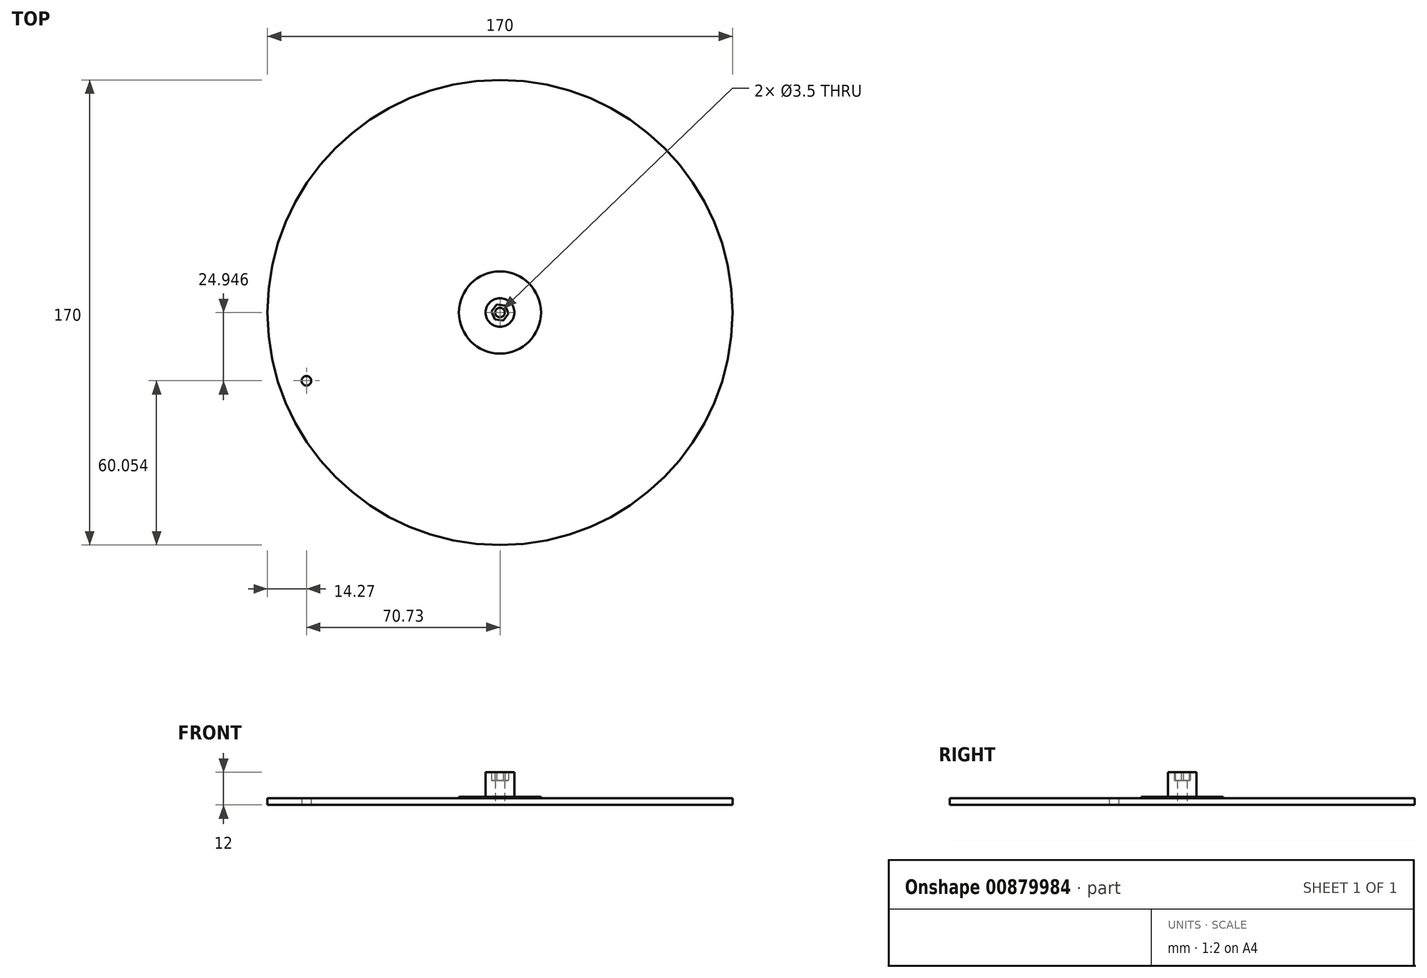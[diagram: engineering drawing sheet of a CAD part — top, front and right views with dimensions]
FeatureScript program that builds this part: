
annotation { "Feature Type Name" : "Feature", "Feature Type Description" : "" }
export const myFeature = defineFeature(function(context is Context, id is Id, definition is map)
    precondition{}
    {
        {
            var Q0;
            Q0=qCreatedBy(makeId("Top.planeOp"),FACE);
            var sketch = newSketch(context, id + "F0", { "sketchPlane" : qUnion([Q0])});
            skCircle(sketch, "E0", {"center": v(0, 0) * mm, "radius": 85 * mm});
            skCircle(sketch, "E1", {"center": v(0, 0) * mm, "radius": 75 * mm, "construction": true});
            skCircle(sketch, "E2", {"center": v(-70.73, -24.95) * mm, "radius": 1.75 * mm});
            skCircle(sketch, "E3", {"center": v(0, 0) * mm, "radius": 5.25 * mm});
            skCircle(sketch, "E4.cCircle", {"center": v(0, 0) * mm, "radius": 2.75 * mm, "construction": true});
            skLineSegment(sketch, "E4.0", {"start": v(1.89, 2.55) * mm, "end": v(3.16, -0.36) * mm});
            skLineSegment(sketch, "E4.1", {"start": v(3.16, -0.36) * mm, "end": v(1.27, -2.91) * mm});
            skLineSegment(sketch, "E4.2", {"start": v(1.27, -2.91) * mm, "end": v(-1.89, -2.55) * mm});
            skLineSegment(sketch, "E4.3", {"start": v(-1.89, -2.55) * mm, "end": v(-3.16, 0.36) * mm});
            skLineSegment(sketch, "E4.4", {"start": v(-3.16, 0.36) * mm, "end": v(-1.27, 2.91) * mm});
            skLineSegment(sketch, "E4.5", {"start": v(-1.27, 2.91) * mm, "end": v(1.89, 2.55) * mm});
            skPoint(sketch, "E4.0.midPoint", {"position": v(2.52, 1.1) * mm});
            skCircle(sketch, "E5", {"center": v(0, 0) * mm, "radius": 1.75 * mm});
            skCircle(sketch, "E6", {"center": v(0, 0) * mm, "radius": 15 * mm});
            skSolve(sketch);
        }
        {
            var Q0;
            Q0=makeQuery(id+"F0.imprint","IMPRINT",FACE,{"disambiguationData":[TD([[makeQuery(id+"F0.imprint","IMPRINT",EDGE,{"derivedFrom":sQuery(id+"F0.wireOp",EDGE,"E0")}),1.0]])]});
            var Q1;
            Q1=makeQuery(id+"F0.imprint","IMPRINT",FACE,{"disambiguationData":[TD([[makeQuery(id+"F0.imprint","IMPRINT",EDGE,{"derivedFrom":sQuery(id+"F0.wireOp",EDGE,"E2")}),1.0]])]});
            var Q2;
            Q2=makeQuery(id+"F0.imprint","IMPRINT",FACE,{"disambiguationData":[TD([[makeQuery(id+"F0.imprint","IMPRINT",EDGE,{"derivedFrom":sQuery(id+"F0.wireOp",EDGE,"E3")}),1.0]])]});
            var Q3;
            Q3=makeQuery(id+"F0.imprint","IMPRINT",FACE,{"disambiguationData":[TD([[makeQuery(id+"F0.imprint","IMPRINT",EDGE,{"derivedFrom":sQuery(id+"F0.wireOp",EDGE,"E4.0")}),-1.0]])]});
            var Q4;
            Q4=makeQuery(id+"F0.imprint","IMPRINT",FACE,{"disambiguationData":[TD([[makeQuery(id+"F0.imprint","IMPRINT",EDGE,{"derivedFrom":sQuery(id+"F0.wireOp",EDGE,"E3")}),-1.0]])]});
            extrude(context, id + "F1", {"entities" : qUnion([Q0, Q1, Q2, Q3, Q4]), "depth" : 2.5 * mm, "offsetDistance" : 25 * mm});
        }
        {
            var Q0;
            Q0=makeQuery(id+"F0.imprint","IMPRINT",FACE,{"disambiguationData":[TD([[makeQuery(id+"F0.imprint","IMPRINT",EDGE,{"derivedFrom":sQuery(id+"F0.wireOp",EDGE,"E2")}),1.0]])]});
            extrude(context, id + "F2", {"entities" : qUnion([Q0]), "operationType" : NewBodyOperationType.REMOVE, "endBound" : BoundingType.UP_TO_NEXT, "depth" : 25 * mm, "offsetDistance" : 25 * mm});
        }
        {
            var Q0;
            Q0=makeQuery(id+"F0.imprint","IMPRINT",FACE,{"disambiguationData":[TD([[makeQuery(id+"F0.imprint","IMPRINT",EDGE,{"derivedFrom":sQuery(id+"F0.wireOp",EDGE,"E3")}),1.0]])]});
            extrude(context, id + "F3", {"entities" : qUnion([Q0]), "operationType" : NewBodyOperationType.ADD, "depth" : 12 * mm, "offsetDistance" : 25 * mm});
        }
        {
            var Q0;
            Q0=makeQuery(id+"F0.imprint","IMPRINT",FACE,{"disambiguationData":[TD([[makeQuery(id+"F0.imprint","IMPRINT",EDGE,{"derivedFrom":sQuery(id+"F0.wireOp",EDGE,"E4.0")}),-1.0]])]});
            extrude(context, id + "F4", {"entities" : qUnion([Q0]), "operationType" : NewBodyOperationType.ADD, "depth" : 9 * mm, "offsetDistance" : 25 * mm});
        }
        {
            var Q0;
            Q0=makeQuery(id+"F0.imprint","IMPRINT",FACE,{"disambiguationData":[TD([[makeQuery(id+"F0.imprint","IMPRINT",EDGE,{"derivedFrom":sQuery(id+"F0.wireOp",EDGE,"E3")}),-1.0]])]});
            extrude(context, id + "F5", {"entities" : qUnion([Q0]), "operationType" : NewBodyOperationType.ADD, "depth" : 3 * mm, "offsetDistance" : 25 * mm});
        }
    });
